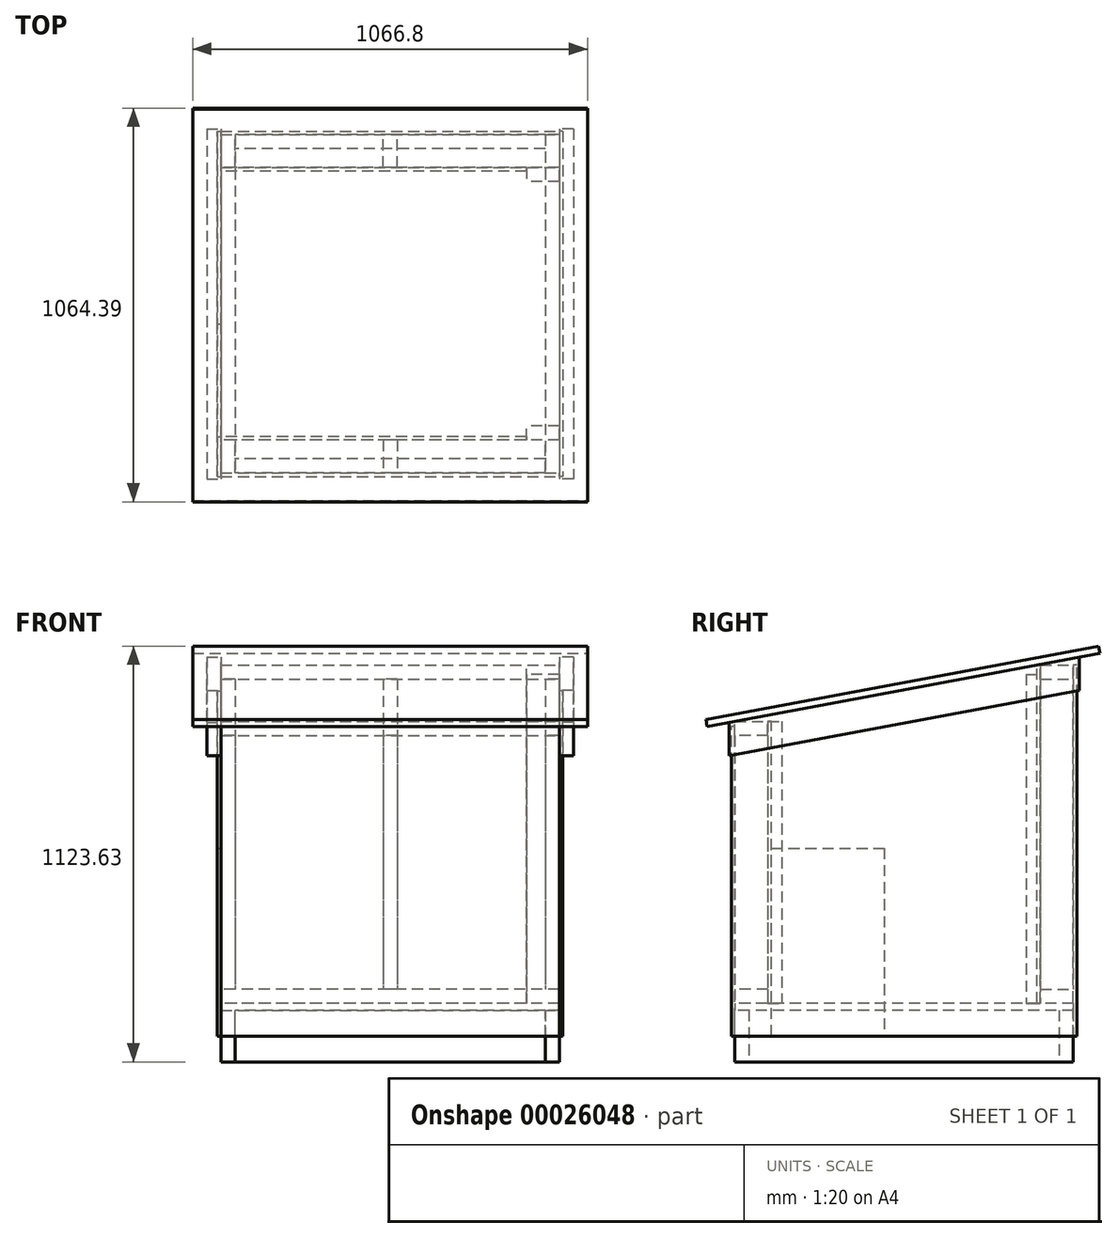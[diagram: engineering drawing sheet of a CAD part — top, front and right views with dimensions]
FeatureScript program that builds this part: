
annotation { "Feature Type Name" : "Feature", "Feature Type Description" : "" }
export const myFeature = defineFeature(function(context is Context, id is Id, definition is map)
    precondition{}
    {
        {
            var Q0;
            Q0=qCreatedBy(makeId("Front.planeOp"),FACE);
            var sketch = newSketch(context, id + "F0", { "sketchPlane" : qUnion([Q0])});
            skLineSegment(sketch, "E0.bottom", {"start": v(0, 0) * mm, "end": v(38.1, 0) * mm});
            skLineSegment(sketch, "E0.top", {"start": v(0, 139.7) * mm, "end": v(38.1, 139.7) * mm});
            skLineSegment(sketch, "E0.left", {"start": v(0, 0) * mm, "end": v(0, 139.7) * mm});
            skLineSegment(sketch, "E0.right", {"start": v(38.1, 0) * mm, "end": v(38.1, 139.7) * mm});
            skSolve(sketch);
        }
        {
            var Q0;
            Q0 = qSketchRegion(id + "F0", true);
            extrude(context, id + "F1", {"entities" : qUnion([Q0]), "oppositeDirection" : true, "depth" : 914.4 * mm});
        }
        {
            var Q0;
            Q0=qCreatedBy(makeId("Front.planeOp"),FACE);
            var sketch = newSketch(context, id + "F2", { "sketchPlane" : qUnion([Q0])});
            skLineSegment(sketch, "E1.bottom", {"start": v(876.3, 0) * mm, "end": v(914.4, 0) * mm});
            skLineSegment(sketch, "E1.top", {"start": v(876.3, 139.7) * mm, "end": v(914.4, 139.7) * mm});
            skLineSegment(sketch, "E1.left", {"start": v(876.3, 0) * mm, "end": v(876.3, 139.7) * mm});
            skLineSegment(sketch, "E1.right", {"start": v(914.4, 0) * mm, "end": v(914.4, 139.7) * mm});
            skSolve(sketch);
        }
        {
            var Q0;
            Q0=makeQuery(id+"F2.imprint","IMPRINT",FACE,{"disambiguationData":[TD([[makeQuery(id+"F2.imprint","IMPRINT",EDGE,{"derivedFrom":sQuery(id+"F2.wireOp",EDGE,"E1.bottom")}),1.0]])]});
            var Q1;
            Q1=makeQuery(id+"F1.opExtrude","CAP_FACE",FACE,{"disambiguationData":[OSD([sQuery(id+"F0.wireOp",EDGE,"E0.bottom"),sQuery(id+"F0.wireOp",EDGE,"E0.top"),sQuery(id+"F0.wireOp",EDGE,"E0.left"),sQuery(id+"F0.wireOp",EDGE,"E0.right")])],"isStart":false});
            extrude(context, id + "F3", {"entities" : qUnion([Q0]), "endBound" : BoundingType.UP_TO_SURFACE, "oppositeDirection" : true, "endBoundEntityFace" : qUnion([Q1]), "depth" : 914.4 * mm});
        }
        {
            var Q0;
            Q0=makeQuery(id+"F1.opExtrude","SWEPT_FACE",FACE,{"disambiguationData":[OSD([sQuery(id+"F0.wireOp",EDGE,"E0.right")])]});
            var sketch = newSketch(context, id + "F4", { "sketchPlane" : qUnion([Q0])});
            skLineSegment(sketch, "E2.bottom", {"start": v(914.4, 139.7) * mm, "end": v(876.3, 139.7) * mm});
            skLineSegment(sketch, "E2.top", {"start": v(914.4, 0) * mm, "end": v(876.3, 0) * mm});
            skLineSegment(sketch, "E2.left", {"start": v(914.4, 139.7) * mm, "end": v(914.4, 0) * mm});
            skLineSegment(sketch, "E2.right", {"start": v(876.3, 139.7) * mm, "end": v(876.3, 0) * mm});
            skSolve(sketch);
        }
        {
            var Q0;
            Q0 = qSketchRegion(id + "F4", true);
            var Q1;
            Q1=makeQuery(id+"F3.opExtrude","SWEPT_BODY",BODY,{"disambiguationData":[OSD([sQuery(id+"F2.wireOp",EDGE,"E1.bottom"),sQuery(id+"F2.wireOp",EDGE,"E1.top"),sQuery(id+"F2.wireOp",EDGE,"E1.left"),sQuery(id+"F2.wireOp",EDGE,"E1.right")])]});
            extrude(context, id + "F5", {"entities" : qUnion([Q0]), "endBound" : BoundingType.UP_TO_BODY, "endBoundEntityBody" : qUnion([Q1]), "depth" : 25.4 * mm});
        }
        {
            var Q0;
            Q0=makeQuery(id+"F1.opExtrude","SWEPT_FACE",FACE,{"disambiguationData":[OSD([sQuery(id+"F0.wireOp",EDGE,"E0.right")])]});
            var sketch = newSketch(context, id + "F6", { "sketchPlane" : qUnion([Q0])});
            skLineSegment(sketch, "E3.bottom", {"start": v(0, 139.7) * mm, "end": v(38.1, 139.7) * mm});
            skLineSegment(sketch, "E3.top", {"start": v(0, 0) * mm, "end": v(38.1, 0) * mm});
            skLineSegment(sketch, "E3.left", {"start": v(0, 139.7) * mm, "end": v(0, 0) * mm});
            skLineSegment(sketch, "E3.right", {"start": v(38.1, 139.7) * mm, "end": v(38.1, 0) * mm});
            skSolve(sketch);
        }
        {
            var Q0;
            Q0 = qSketchRegion(id + "F6", true);
            var Q1;
            Q1=makeQuery(id+"F3.opExtrude","SWEPT_BODY",BODY,{"disambiguationData":[OSD([sQuery(id+"F2.wireOp",EDGE,"E1.bottom"),sQuery(id+"F2.wireOp",EDGE,"E1.top"),sQuery(id+"F2.wireOp",EDGE,"E1.left"),sQuery(id+"F2.wireOp",EDGE,"E1.right")])]});
            extrude(context, id + "F7", {"entities" : qUnion([Q0]), "endBound" : BoundingType.UP_TO_BODY, "endBoundEntityBody" : qUnion([Q1]), "depth" : 25.4 * mm});
        }
        {
            var Q0;
            Q0=makeQuery(id+"F1.opExtrude","SWEPT_FACE",FACE,{"disambiguationData":[OSD([sQuery(id+"F0.wireOp",EDGE,"E0.top")])]});
            var sketch = newSketch(context, id + "F8", { "sketchPlane" : qUnion([Q0])});
            skLineSegment(sketch, "E4.bottom", {"start": v(0, 0) * mm, "end": v(914.4, 0) * mm});
            skLineSegment(sketch, "E4.top", {"start": v(0, 914.4) * mm, "end": v(914.4, 914.4) * mm});
            skLineSegment(sketch, "E4.left", {"start": v(0, 0) * mm, "end": v(0, 914.4) * mm});
            skLineSegment(sketch, "E4.right", {"start": v(914.4, 0) * mm, "end": v(914.4, 914.4) * mm});
            skSolve(sketch);
        }
        {
            var Q0;
            Q0 = qSketchRegion(id + "F8", true);
            extrude(context, id + "F9", {"entities" : qUnion([Q0]), "depth" : 19.05 * mm});
        }
        {
            var Q0;
            Q0=makeQuery(id+"F1.opExtrude","SWEPT_FACE",FACE,{"disambiguationData":[OSD([sQuery(id+"F0.wireOp",EDGE,"E0.left")])]});
            var sketch = newSketch(context, id + "F10", { "sketchPlane" : qUnion([Q0])});
            skLineSegment(sketch, "E5.bottom", {"start": v(0, 158.75) * mm, "end": v(-88.9, 158.75) * mm});
            skLineSegment(sketch, "E5.top", {"start": v(0, 196.85) * mm, "end": v(-88.9, 196.85) * mm});
            skLineSegment(sketch, "E5.left", {"start": v(0, 158.75) * mm, "end": v(0, 196.85) * mm});
            skLineSegment(sketch, "E5.right", {"start": v(-88.9, 158.75) * mm, "end": v(-88.9, 196.85) * mm});
            skSolve(sketch);
        }
        {
            var Q0;
            Q0 = qSketchRegion(id + "F10", true);
            var Q1;
            Q1=makeQuery(id+"F9.opExtrude","SWEPT_FACE",FACE,{"disambiguationData":[OSD([sQuery(id+"F8.wireOp",EDGE,"E4.right")])]});
            extrude(context, id + "F11", {"entities" : qUnion([Q0]), "endBound" : BoundingType.UP_TO_SURFACE, "oppositeDirection" : true, "endBoundEntityFace" : qUnion([Q1]), "depth" : 25.4 * mm});
        }
        {
            var Q0;
            Q0=makeQuery(id+"F1.opExtrude","SWEPT_FACE",FACE,{"disambiguationData":[OSD([sQuery(id+"F0.wireOp",EDGE,"E0.left")])]});
            var sketch = newSketch(context, id + "F12", { "sketchPlane" : qUnion([Q0])});
            skLineSegment(sketch, "E6.bottom", {"start": v(-914.4, 158.75) * mm, "end": v(-825.5, 158.75) * mm});
            skLineSegment(sketch, "E6.top", {"start": v(-914.4, 196.85) * mm, "end": v(-825.5, 196.85) * mm});
            skLineSegment(sketch, "E6.left", {"start": v(-914.4, 158.75) * mm, "end": v(-914.4, 196.85) * mm});
            skLineSegment(sketch, "E6.right", {"start": v(-825.5, 158.75) * mm, "end": v(-825.5, 196.85) * mm});
            skSolve(sketch);
        }
        {
            var Q0;
            Q0 = qSketchRegion(id + "F12", true);
            var Q1;
            Q1=makeQuery(id+"F3.opExtrude","SWEPT_FACE",FACE,{"disambiguationData":[OSD([sQuery(id+"F2.wireOp",EDGE,"E1.right")])]});
            extrude(context, id + "F13", {"entities" : qUnion([Q0]), "endBound" : BoundingType.UP_TO_SURFACE, "oppositeDirection" : true, "endBoundEntityFace" : qUnion([Q1]), "depth" : 25.4 * mm});
        }
        {
            var Q0;
            Q0=makeQuery(id+"F13.opExtrude","SWEPT_FACE",FACE,{"disambiguationData":[OSD([sQuery(id+"F12.wireOp",EDGE,"E6.top")])]});
            var sketch = newSketch(context, id + "F14", { "sketchPlane" : qUnion([Q0])});
            skLineSegment(sketch, "E7.bottom", {"start": v(914.4, 914.4) * mm, "end": v(876.3, 914.4) * mm});
            skLineSegment(sketch, "E7.top", {"start": v(914.4, 825.5) * mm, "end": v(876.3, 825.5) * mm});
            skLineSegment(sketch, "E7.left", {"start": v(914.4, 914.4) * mm, "end": v(914.4, 825.5) * mm});
            skLineSegment(sketch, "E7.right", {"start": v(876.3, 914.4) * mm, "end": v(876.3, 825.5) * mm});
            skSolve(sketch);
        }
        {
            var Q0;
            Q0 = qSketchRegion(id + "F14", true);
            extrude(context, id + "F15", {"entities" : qUnion([Q0]), "depth" : 838.2 * mm});
        }
        {
            var Q0;
            Q0=makeQuery(id+"F13.opExtrude","SWEPT_FACE",FACE,{"disambiguationData":[OSD([sQuery(id+"F12.wireOp",EDGE,"E6.top")])]});
            var sketch = newSketch(context, id + "F16", { "sketchPlane" : qUnion([Q0])});
            skLineSegment(sketch, "E8.bottom", {"start": v(0, 825.5) * mm, "end": v(38.1, 825.5) * mm});
            skLineSegment(sketch, "E8.top", {"start": v(0, 914.4) * mm, "end": v(38.1, 914.4) * mm});
            skLineSegment(sketch, "E8.left", {"start": v(0, 825.5) * mm, "end": v(0, 914.4) * mm});
            skLineSegment(sketch, "E8.right", {"start": v(38.1, 825.5) * mm, "end": v(38.1, 914.4) * mm});
            skSolve(sketch);
        }
        {
            var Q0;
            Q0 = qSketchRegion(id + "F16", true);
            var Q1;
            Q1=makeQuery(id+"F15.opExtrude","CAP_FACE",FACE,{"disambiguationData":[OSD([sQuery(id+"F14.wireOp",EDGE,"E7.bottom"),sQuery(id+"F14.wireOp",EDGE,"E7.top"),sQuery(id+"F14.wireOp",EDGE,"E7.left"),sQuery(id+"F14.wireOp",EDGE,"E7.right")])],"isStart":false});
            extrude(context, id + "F17", {"entities" : qUnion([Q0]), "endBound" : BoundingType.UP_TO_SURFACE, "endBoundEntityFace" : qUnion([Q1]), "depth" : 25.4 * mm});
        }
        {
            var Q0;
            Q0=makeQuery(id+"F13.opExtrude","SWEPT_FACE",FACE,{"disambiguationData":[OSD([sQuery(id+"F12.wireOp",EDGE,"E6.top")])]});
            var sketch = newSketch(context, id + "F18", { "sketchPlane" : qUnion([Q0])});
            skLineSegment(sketch, "E9.bottom", {"start": v(438.15, 825.5) * mm, "end": v(476.25, 825.5) * mm});
            skLineSegment(sketch, "E9.top", {"start": v(438.15, 914.4) * mm, "end": v(476.25, 914.4) * mm});
            skLineSegment(sketch, "E9.left", {"start": v(438.15, 825.5) * mm, "end": v(438.15, 914.4) * mm});
            skLineSegment(sketch, "E9.right", {"start": v(476.25, 825.5) * mm, "end": v(476.25, 914.4) * mm});
            skSolve(sketch);
        }
        {
            var Q0;
            Q0 = qSketchRegion(id + "F18", true);
            var Q1;
            Q1=makeQuery(id+"F15.opExtrude","CAP_FACE",FACE,{"disambiguationData":[OSD([sQuery(id+"F14.wireOp",EDGE,"E7.bottom"),sQuery(id+"F14.wireOp",EDGE,"E7.top"),sQuery(id+"F14.wireOp",EDGE,"E7.left"),sQuery(id+"F14.wireOp",EDGE,"E7.right")])],"isStart":false});
            extrude(context, id + "F19", {"entities" : qUnion([Q0]), "endBound" : BoundingType.UP_TO_SURFACE, "endBoundEntityFace" : qUnion([Q1]), "depth" : 25.4 * mm});
        }
        {
            var Q0;
            Q0=makeQuery(id+"F15.opExtrude","SWEPT_FACE",FACE,{"disambiguationData":[OSD([sQuery(id+"F14.wireOp",EDGE,"E7.left")])]});
            var sketch = newSketch(context, id + "F20", { "sketchPlane" : qUnion([Q0])});
            skLineSegment(sketch, "E10.bottom", {"start": v(914.4, 1035.05) * mm, "end": v(825.5, 1035.05) * mm});
            skLineSegment(sketch, "E10.top", {"start": v(914.4, 1073.15) * mm, "end": v(825.5, 1073.15) * mm});
            skLineSegment(sketch, "E10.left", {"start": v(914.4, 1035.05) * mm, "end": v(914.4, 1073.15) * mm});
            skLineSegment(sketch, "E10.right", {"start": v(825.5, 1035.05) * mm, "end": v(825.5, 1073.15) * mm});
            skSolve(sketch);
        }
        {
            var Q0;
            Q0 = qSketchRegion(id + "F20", true);
            var Q1;
            Q1=makeQuery(id+"F17.opExtrude","SWEPT_FACE",FACE,{"disambiguationData":[OSD([sQuery(id+"F16.wireOp",EDGE,"E8.left")])]});
            extrude(context, id + "F21", {"entities" : qUnion([Q0]), "endBound" : BoundingType.UP_TO_SURFACE, "oppositeDirection" : true, "endBoundEntityFace" : qUnion([Q1]), "depth" : 25.4 * mm});
        }
        {
            var Q0;
            Q0=makeQuery(id+"F11.opExtrude","SWEPT_FACE",FACE,{"disambiguationData":[OSD([sQuery(id+"F10.wireOp",EDGE,"E5.top")])]});
            var sketch = newSketch(context, id + "F22", { "sketchPlane" : qUnion([Q0])});
            skLineSegment(sketch, "E11.bottom", {"start": v(914.4, 0) * mm, "end": v(876.3, 0) * mm});
            skLineSegment(sketch, "E11.top", {"start": v(914.4, 88.9) * mm, "end": v(876.3, 88.9) * mm});
            skLineSegment(sketch, "E11.left", {"start": v(914.4, 0) * mm, "end": v(914.4, 88.9) * mm});
            skLineSegment(sketch, "E11.right", {"start": v(876.3, 0) * mm, "end": v(876.3, 88.9) * mm});
            skSolve(sketch);
        }
        {
            var Q0;
            Q0 = qSketchRegion(id + "F22", true);
            extrude(context, id + "F23", {"entities" : qUnion([Q0]), "depth" : 685.8 * mm});
        }
        {
            var Q0;
            Q0=makeQuery(id+"F11.opExtrude","SWEPT_FACE",FACE,{"disambiguationData":[OSD([sQuery(id+"F10.wireOp",EDGE,"E5.top")])]});
            var sketch = newSketch(context, id + "F24", { "sketchPlane" : qUnion([Q0])});
            skLineSegment(sketch, "E12.bottom", {"start": v(0, 0) * mm, "end": v(38.1, 0) * mm});
            skLineSegment(sketch, "E12.top", {"start": v(0, 88.9) * mm, "end": v(38.1, 88.9) * mm});
            skLineSegment(sketch, "E12.left", {"start": v(0, 0) * mm, "end": v(0, 88.9) * mm});
            skLineSegment(sketch, "E12.right", {"start": v(38.1, 0) * mm, "end": v(38.1, 88.9) * mm});
            skSolve(sketch);
        }
        {
            var Q0;
            Q0 = qSketchRegion(id + "F24", true);
            var Q1;
            Q1=makeQuery(id+"F23.opExtrude","CAP_FACE",FACE,{"disambiguationData":[OSD([sQuery(id+"F22.wireOp",EDGE,"E11.bottom"),sQuery(id+"F22.wireOp",EDGE,"E11.top"),sQuery(id+"F22.wireOp",EDGE,"E11.left"),sQuery(id+"F22.wireOp",EDGE,"E11.right")])],"isStart":false});
            extrude(context, id + "F25", {"entities" : qUnion([Q0]), "endBound" : BoundingType.UP_TO_SURFACE, "endBoundEntityFace" : qUnion([Q1]), "depth" : 25.4 * mm});
        }
        {
            var Q0;
            Q0=makeQuery(id+"F11.opExtrude","SWEPT_FACE",FACE,{"disambiguationData":[OSD([sQuery(id+"F10.wireOp",EDGE,"E5.top")])]});
            var sketch = newSketch(context, id + "F26", { "sketchPlane" : qUnion([Q0])});
            skLineSegment(sketch, "E13.bottom", {"start": v(438.15, 88.9) * mm, "end": v(476.25, 88.9) * mm});
            skLineSegment(sketch, "E13.top", {"start": v(438.15, 0) * mm, "end": v(476.25, 0) * mm});
            skLineSegment(sketch, "E13.left", {"start": v(438.15, 88.9) * mm, "end": v(438.15, 0) * mm});
            skLineSegment(sketch, "E13.right", {"start": v(476.25, 88.9) * mm, "end": v(476.25, 0) * mm});
            skSolve(sketch);
        }
        {
            var Q0;
            Q0 = qSketchRegion(id + "F26", true);
            var Q1;
            Q1=makeQuery(id+"F23.opExtrude","CAP_FACE",FACE,{"disambiguationData":[OSD([sQuery(id+"F22.wireOp",EDGE,"E11.bottom"),sQuery(id+"F22.wireOp",EDGE,"E11.top"),sQuery(id+"F22.wireOp",EDGE,"E11.left"),sQuery(id+"F22.wireOp",EDGE,"E11.right")])],"isStart":false});
            extrude(context, id + "F27", {"entities" : qUnion([Q0]), "endBound" : BoundingType.UP_TO_SURFACE, "endBoundEntityFace" : qUnion([Q1]), "depth" : 25.4 * mm});
        }
        {
            var Q0;
            Q0=makeQuery(id+"F23.opExtrude","SWEPT_FACE",FACE,{"disambiguationData":[OSD([sQuery(id+"F22.wireOp",EDGE,"E11.left")])]});
            var sketch = newSketch(context, id + "F28", { "sketchPlane" : qUnion([Q0])});
            skLineSegment(sketch, "E14.bottom", {"start": v(0, 882.65) * mm, "end": v(88.9, 882.65) * mm});
            skLineSegment(sketch, "E14.top", {"start": v(0, 920.75) * mm, "end": v(88.9, 920.75) * mm});
            skLineSegment(sketch, "E14.left", {"start": v(0, 882.65) * mm, "end": v(0, 920.75) * mm});
            skLineSegment(sketch, "E14.right", {"start": v(88.9, 882.65) * mm, "end": v(88.9, 920.75) * mm});
            skSolve(sketch);
        }
        {
            var Q0;
            Q0 = qSketchRegion(id + "F28", true);
            var Q1;
            Q1=makeQuery(id+"F25.opExtrude","SWEPT_FACE",FACE,{"disambiguationData":[OSD([sQuery(id+"F24.wireOp",EDGE,"E12.left")])]});
            extrude(context, id + "F29", {"entities" : qUnion([Q0]), "endBound" : BoundingType.UP_TO_SURFACE, "oppositeDirection" : true, "endBoundEntityFace" : qUnion([Q1]), "depth" : 25.4 * mm});
        }
        {
            var Q0;
            Q0=makeQuery(id+"F13.opExtrude","SWEPT_FACE",FACE,{"disambiguationData":[OSD([sQuery(id+"F12.wireOp",EDGE,"E6.right")])]});
            var sketch = newSketch(context, id + "F30", { "sketchPlane" : qUnion([Q0])});
            skLineSegment(sketch, "E15.bottom", {"start": v(0, 158.75) * mm, "end": v(825.5, 158.75) * mm});
            skLineSegment(sketch, "E15.top", {"start": v(0, 1073.15) * mm, "end": v(825.5, 1073.15) * mm});
            skLineSegment(sketch, "E15.left", {"start": v(0, 158.75) * mm, "end": v(0, 1073.15) * mm});
            skLineSegment(sketch, "E15.right", {"start": v(825.5, 158.75) * mm, "end": v(825.5, 1073.15) * mm});
            skSolve(sketch);
        }
        {
            var Q0;
            Q0 = qSketchRegion(id + "F30", true);
            extrude(context, id + "F31", {"entities" : qUnion([Q0]), "depth" : 9.52 * mm});
        }
        {
            var Q0;
            Q0=makeQuery(id+"F11.opExtrude","SWEPT_FACE",FACE,{"disambiguationData":[OSD([sQuery(id+"F10.wireOp",EDGE,"E5.right")])]});
            var sketch = newSketch(context, id + "F32", { "sketchPlane" : qUnion([Q0])});
            skLineSegment(sketch, "E16.bottom", {"start": v(0, 158.75) * mm, "end": v(-825.5, 158.75) * mm});
            skLineSegment(sketch, "E16.top", {"start": v(0, 920.75) * mm, "end": v(-825.5, 920.75) * mm});
            skLineSegment(sketch, "E16.left", {"start": v(0, 158.75) * mm, "end": v(0, 920.75) * mm});
            skLineSegment(sketch, "E16.right", {"start": v(-825.5, 158.75) * mm, "end": v(-825.5, 920.75) * mm});
            skSolve(sketch);
        }
        {
            var Q0;
            Q0 = qSketchRegion(id + "F32", true);
            extrude(context, id + "F33", {"entities" : qUnion([Q0]), "depth" : 9.52 * mm});
        }
        {
            var Q0;
            Q0=makeQuery(id+"F31.opExtrude","CAP_VERTEX",VERTEX,{"disambiguationData":[OSD([sQuery(id+"F30.wireOp",EDGE,"E15.top"),sQuery(id+"F30.wireOp",EDGE,"E15.left")])],"isStart":false});
            var Q1;
            Q1=makeQuery(id+"F31.opExtrude","CAP_VERTEX",VERTEX,{"disambiguationData":[OSD([sQuery(id+"F30.wireOp",EDGE,"E15.top"),sQuery(id+"F30.wireOp",EDGE,"E15.right")])],"isStart":false});
            var Q2;
            Q2=makeQuery(id+"F29.opExtrude","CAP_VERTEX",VERTEX,{"disambiguationData":[OSD([sQuery(id+"F28.wireOp",EDGE,"E14.top"),sQuery(id+"F28.wireOp",EDGE,"E14.left")])],"isStart":true});
            cPlane(context, id + "F34", {"entities" : qUnion([Q0, Q1, Q2]), "cplaneType" : CPlaneType.THREE_POINT, "offset" : 152.4 * mm, "width" : 152.4 * mm, "height" : 152.4 * mm});
        }
        {
            var Q0;
            Q0=qCreatedBy(id+"F34.planeOp",FACE);
            var sketch = newSketch(context, id + "F35", { "sketchPlane" : qUnion([Q0])});
            skLineSegment(sketch, "E17.bottom", {"start": v(-76.2, 92.85) * mm, "end": v(990.6, 92.85) * mm});
            skLineSegment(sketch, "E17.top", {"start": v(-76.2, 1172.08) * mm, "end": v(990.6, 1172.08) * mm});
            skLineSegment(sketch, "E17.left", {"start": v(-76.2, 92.85) * mm, "end": v(-76.2, 1172.08) * mm});
            skLineSegment(sketch, "E17.right", {"start": v(990.6, 92.85) * mm, "end": v(990.6, 1172.08) * mm});
            skSolve(sketch);
        }
        {
            var Q0;
            Q0 = qSketchRegion(id + "F35", true);
            extrude(context, id + "F36", {"entities" : qUnion([Q0]), "depth" : 19.05 * mm});
        }
        {
            var Q0;
            Q0=makeQuery(id+"F1.opExtrude","CAP_FACE",FACE,{"disambiguationData":[OSD([sQuery(id+"F0.wireOp",EDGE,"E0.bottom"),sQuery(id+"F0.wireOp",EDGE,"E0.top"),sQuery(id+"F0.wireOp",EDGE,"E0.left"),sQuery(id+"F0.wireOp",EDGE,"E0.right")])],"isStart":false});
            var sketch = newSketch(context, id + "F37", { "sketchPlane" : qUnion([Q0])});
            skLineSegment(sketch, "E18.bottom", {"start": v(0, 69.85) * mm, "end": v(-914.4, 69.85) * mm});
            skLineSegment(sketch, "E18.top", {"start": v(0, 1073.15) * mm, "end": v(-914.4, 1073.15) * mm});
            skLineSegment(sketch, "E18.left", {"start": v(0, 69.85) * mm, "end": v(0, 1073.15) * mm});
            skLineSegment(sketch, "E18.right", {"start": v(-914.4, 69.85) * mm, "end": v(-914.4, 1073.15) * mm});
            skSolve(sketch);
        }
        {
            var Q0;
            Q0 = qSketchRegion(id + "F37", true);
            extrude(context, id + "F38", {"entities" : qUnion([Q0]), "depth" : 9.52 * mm});
        }
        {
            var Q0;
            Q0=makeQuery(id+"F1.opExtrude","CAP_FACE",FACE,{"disambiguationData":[OSD([sQuery(id+"F0.wireOp",EDGE,"E0.bottom"),sQuery(id+"F0.wireOp",EDGE,"E0.top"),sQuery(id+"F0.wireOp",EDGE,"E0.left"),sQuery(id+"F0.wireOp",EDGE,"E0.right")])],"isStart":true});
            var sketch = newSketch(context, id + "F39", { "sketchPlane" : qUnion([Q0])});
            skLineSegment(sketch, "E19.bottom", {"start": v(0, 69.85) * mm, "end": v(914.4, 69.85) * mm});
            skLineSegment(sketch, "E19.top", {"start": v(0, 908.05) * mm, "end": v(914.4, 908.05) * mm});
            skLineSegment(sketch, "E19.left", {"start": v(0, 69.85) * mm, "end": v(0, 908.05) * mm});
            skLineSegment(sketch, "E19.right", {"start": v(914.4, 69.85) * mm, "end": v(914.4, 908.05) * mm});
            skSolve(sketch);
        }
        {
            var Q0;
            Q0 = qSketchRegion(id + "F39", true);
            extrude(context, id + "F40", {"entities" : qUnion([Q0]), "depth" : 9.52 * mm});
        }
        {
            var Q0;
            Q0=makeQuery(id+"F21.opExtrude","CAP_FACE",FACE,{"disambiguationData":[OSD([sQuery(id+"F20.wireOp",EDGE,"E10.bottom"),sQuery(id+"F20.wireOp",EDGE,"E10.top"),sQuery(id+"F20.wireOp",EDGE,"E10.left"),sQuery(id+"F20.wireOp",EDGE,"E10.right")])],"isStart":false});
            var sketch = newSketch(context, id + "F41", { "sketchPlane" : qUnion([Q0])});
            skLineSegment(sketch, "E20", {"start": v(-930.28, 1094.5) * mm, "end": v(15.87, 917.79) * mm});
            skLineSegment(sketch, "E21", {"start": v(15.87, 917.79) * mm, "end": v(15.87, 827.35) * mm});
            skLineSegment(sketch, "E22", {"start": v(15.87, 827.35) * mm, "end": v(-930.27, 1004.06) * mm});
            skLineSegment(sketch, "E23", {"start": v(-930.28, 1004.06) * mm, "end": v(-930.28, 1094.5) * mm});
            skSolve(sketch);
        }
        {
            var Q0;
            Q0 = qSketchRegion(id + "F41", true);
            extrude(context, id + "F42", {"entities" : qUnion([Q0]), "depth" : 38.1 * mm});
        }
        {
            var Q0;
            Q0=makeQuery(id+"F21.opExtrude","CAP_FACE",FACE,{"disambiguationData":[OSD([sQuery(id+"F20.wireOp",EDGE,"E10.bottom"),sQuery(id+"F20.wireOp",EDGE,"E10.top"),sQuery(id+"F20.wireOp",EDGE,"E10.left"),sQuery(id+"F20.wireOp",EDGE,"E10.right")])],"isStart":true});
            var sketch = newSketch(context, id + "F43", { "sketchPlane" : qUnion([Q0])});
            skLineSegment(sketch, "E24", {"start": v(-15.88, 917.79) * mm, "end": v(-15.87, 827.35) * mm});
            skLineSegment(sketch, "E25", {"start": v(-15.88, 827.35) * mm, "end": v(930.28, 1004.06) * mm});
            skLineSegment(sketch, "E26", {"start": v(930.28, 1004.06) * mm, "end": v(930.28, 1094.5) * mm});
            skLineSegment(sketch, "E27", {"start": v(930.28, 1094.5) * mm, "end": v(-15.88, 917.79) * mm});
            skSolve(sketch);
        }
        {
            var Q0;
            Q0 = qSketchRegion(id + "F43", true);
            extrude(context, id + "F44", {"entities" : qUnion([Q0]), "depth" : 38.1 * mm});
        }
        {
            var Q0;
            Q0=makeQuery(id+"F9.opExtrude","CAP_FACE",FACE,{"disambiguationData":[OSD([sQuery(id+"F8.wireOp",EDGE,"E4.bottom"),sQuery(id+"F8.wireOp",EDGE,"E4.top"),sQuery(id+"F8.wireOp",EDGE,"E4.left"),sQuery(id+"F8.wireOp",EDGE,"E4.right")])],"isStart":false});
            var sketch = newSketch(context, id + "F45", { "sketchPlane" : qUnion([Q0])});
            skLineSegment(sketch, "E28.bottom", {"start": v(914.4, 825.5) * mm, "end": v(825.5, 825.5) * mm});
            skLineSegment(sketch, "E28.top", {"start": v(914.4, 787.4) * mm, "end": v(825.5, 787.4) * mm});
            skLineSegment(sketch, "E28.left", {"start": v(914.4, 825.5) * mm, "end": v(914.4, 787.4) * mm});
            skLineSegment(sketch, "E28.right", {"start": v(825.5, 825.5) * mm, "end": v(825.5, 787.4) * mm});
            skSolve(sketch);
        }
        {
            var Q0;
            Q0 = qSketchRegion(id + "F45", true);
            extrude(context, id + "F46", {"entities" : qUnion([Q0]), "depth" : 889 * mm});
        }
        {
            var Q0;
            Q0=makeQuery(id+"F9.opExtrude","CAP_FACE",FACE,{"disambiguationData":[OSD([sQuery(id+"F8.wireOp",EDGE,"E4.bottom"),sQuery(id+"F8.wireOp",EDGE,"E4.top"),sQuery(id+"F8.wireOp",EDGE,"E4.left"),sQuery(id+"F8.wireOp",EDGE,"E4.right")])],"isStart":false});
            var sketch = newSketch(context, id + "F47", { "sketchPlane" : qUnion([Q0])});
            skLineSegment(sketch, "E29.bottom", {"start": v(914.4, 88.9) * mm, "end": v(825.5, 88.9) * mm});
            skLineSegment(sketch, "E29.top", {"start": v(914.4, 127) * mm, "end": v(825.5, 127) * mm});
            skLineSegment(sketch, "E29.left", {"start": v(914.4, 88.9) * mm, "end": v(914.4, 127) * mm});
            skLineSegment(sketch, "E29.right", {"start": v(825.5, 88.9) * mm, "end": v(825.5, 127) * mm});
            skSolve(sketch);
        }
        {
            var Q0;
            Q0 = qSketchRegion(id + "F47", true);
            extrude(context, id + "F48", {"entities" : qUnion([Q0]), "depth" : 762 * mm});
        }
        {
            var Q0;
            Q0=makeQuery(id+"F3.opExtrude","SWEPT_FACE",FACE,{"disambiguationData":[OSD([sQuery(id+"F2.wireOp",EDGE,"E1.right")])]});
            var sketch = newSketch(context, id + "F49", { "sketchPlane" : qUnion([Q0])});
            skLineSegment(sketch, "E30.bottom", {"start": v(-9.52, 69.85) * mm, "end": v(923.93, 69.85) * mm});
            skLineSegment(sketch, "E30.left", {"start": v(-9.52, 69.85) * mm, "end": v(-9.53, 828.53) * mm});
            skLineSegment(sketch, "E30.right", {"start": v(923.93, 69.85) * mm, "end": v(923.92, 828.53) * mm});
            skLineSegment(sketch, "E31", {"start": v(-9.53, 828.53) * mm, "end": v(923.93, 1002.87) * mm});
            skLineSegment(sketch, "E32", {"start": v(923.93, 1002.87) * mm, "end": v(923.93, 828.53) * mm});
            skSolve(sketch);
        }
        {
            var Q0;
            Q0 = qSketchRegion(id + "F49", true);
            extrude(context, id + "F50", {"entities" : qUnion([Q0]), "depth" : 9.52 * mm});
        }
        {
            var Q0;
            Q0=makeQuery(id+"F3.opExtrude","SWEPT_FACE",FACE,{"disambiguationData":[OSD([sQuery(id+"F2.wireOp",EDGE,"E1.right")])]});
            var sketch = newSketch(context, id + "F51", { "sketchPlane" : qUnion([Q0])});
            skLineSegment(sketch, "E33.bottom", {"start": v(-9.53, 828.53) * mm, "end": v(923.93, 828.53) * mm});
            skLineSegment(sketch, "E33.top", {"start": v(-9.53, 69.85) * mm, "end": v(923.93, 69.85) * mm});
            skLineSegment(sketch, "E33.left", {"start": v(-9.53, 828.53) * mm, "end": v(-9.52, 69.85) * mm});
            skLineSegment(sketch, "E33.right", {"start": v(923.93, 828.53) * mm, "end": v(923.93, 69.85) * mm});
            skLineSegment(sketch, "E34", {"start": v(923.93, 828.53) * mm, "end": v(923.93, 1002.87) * mm});
            skLineSegment(sketch, "E35", {"start": v(923.93, 1002.87) * mm, "end": v(-9.53, 828.53) * mm});
            skSolve(sketch);
        }
        {
            var Q0;
            Q0 = qSketchRegion(id + "F51", true);
            extrude(context, id + "F52", {"entities" : qUnion([Q0]), "depth" : 9.52 * mm});
        }
        {
            var Q0;
            Q0=makeQuery(id+"F1.opExtrude","SWEPT_FACE",FACE,{"disambiguationData":[OSD([sQuery(id+"F0.wireOp",EDGE,"E0.left")])]});
            var sketch = newSketch(context, id + "F53", { "sketchPlane" : qUnion([Q0])});
            skLineSegment(sketch, "E36", {"start": v(-923.93, 69.85) * mm, "end": v(-923.93, 1002.87) * mm});
            skLineSegment(sketch, "E37", {"start": v(-923.93, 1002.87) * mm, "end": v(9.53, 828.53) * mm});
            skLineSegment(sketch, "E38", {"start": v(9.52, 828.53) * mm, "end": v(9.53, 69.85) * mm});
            skLineSegment(sketch, "E39", {"start": v(9.53, 69.85) * mm, "end": v(-98.42, 69.85) * mm});
            skLineSegment(sketch, "E40", {"start": v(-98.42, 69.85) * mm, "end": v(-98.42, 577.85) * mm});
            skLineSegment(sketch, "E41", {"start": v(-98.42, 577.85) * mm, "end": v(-403.23, 577.85) * mm});
            skLineSegment(sketch, "E42", {"start": v(-403.23, 577.85) * mm, "end": v(-403.22, 69.85) * mm});
            skLineSegment(sketch, "E43", {"start": v(-403.22, 69.85) * mm, "end": v(-923.93, 69.85) * mm});
            skSolve(sketch);
        }
        {
            var Q0;
            Q0 = qSketchRegion(id + "F53", true);
            extrude(context, id + "F54", {"entities" : qUnion([Q0]), "depth" : 9.52 * mm});
        }
    });
